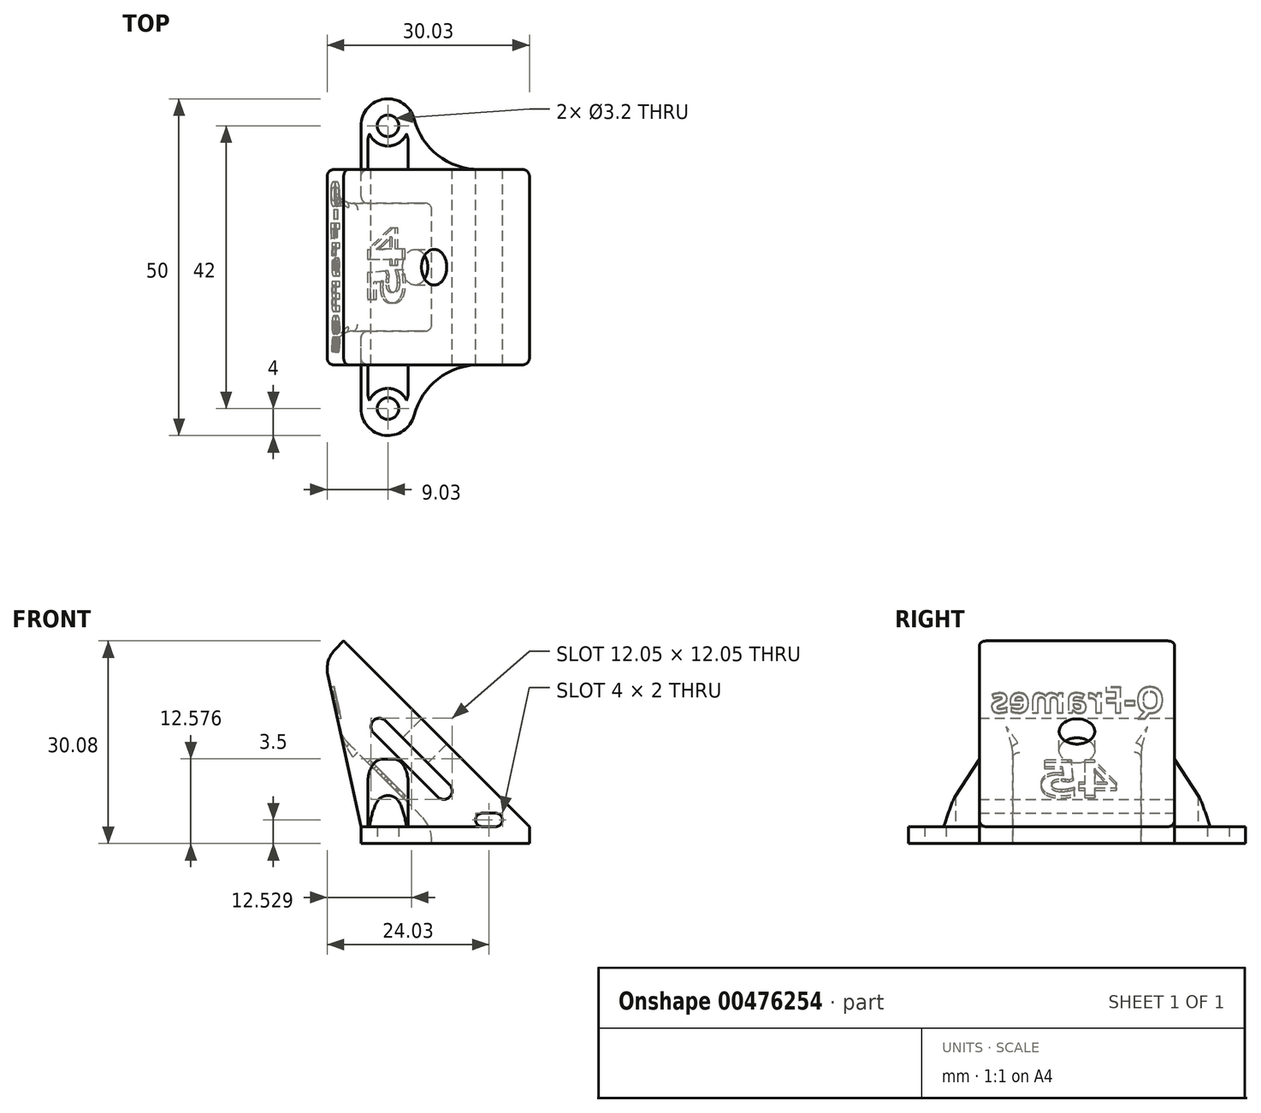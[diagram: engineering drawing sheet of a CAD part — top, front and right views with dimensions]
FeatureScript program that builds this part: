
annotation { "Feature Type Name" : "Feature", "Feature Type Description" : "" }
export const myFeature = defineFeature(function(context is Context, id is Id, definition is map)
    precondition{}
    {
        {
            var Q0;
            Q0=qCreatedBy(makeId("Front.planeOp"),FACE);
            var sketch = newSketch(context, id + "F0", { "sketchPlane" : qUnion([Q0])});
            skLineSegment(sketch, "E0", {"start": v(-27.58, 30.08) * mm, "end": v(0, 2.5) * mm});
            skLineSegment(sketch, "E1", {"start": v(-27.58, 30.08) * mm, "end": v(-28.86, 28.8) * mm});
            skLineSegment(sketch, "E2", {"start": v(-29.94, 25.11) * mm, "end": v(-25, 2.5) * mm});
            skLineSegment(sketch, "E3", {"start": v(0, 0) * mm, "end": v(0, 2.5) * mm});
            skLineSegment(sketch, "E4", {"start": v(-23.16, 18.23) * mm, "end": v(-23.16, 18.23) * mm});
            skLineSegment(sketch, "E5", {"start": v(-23.16, 16.47) * mm, "end": v(-13.61, 6.92) * mm});
            skLineSegment(sketch, "E6", {"start": v(-11.84, 6.92) * mm, "end": v(-11.84, 6.92) * mm});
            skLineSegment(sketch, "E7", {"start": v(-11.84, 8.69) * mm, "end": v(-21.39, 18.23) * mm});
            skLineSegment(sketch, "E8", {"start": v(-13.79, 16.29) * mm, "end": v(-16.62, 13.46) * mm, "construction": true});
            skPoint(sketch, "E9.visualSharp", {"position": v(-22.27, 19.12) * mm});
            skArc(sketch, "E9.filletArc", {"start": v(-21.39, 18.23) * mm, "mid": v(-22.27, 18.6) * mm, "end": v(-23.16, 18.23) * mm});
            skPoint(sketch, "E10.visualSharp", {"position": v(-10.96, 7.8) * mm});
            skArc(sketch, "E10.filletArc", {"start": v(-11.84, 6.92) * mm, "mid": v(-11.48, 7.8) * mm, "end": v(-11.84, 8.69) * mm});
            skPoint(sketch, "E11.visualSharp", {"position": v(-12.73, 6.04) * mm});
            skArc(sketch, "E11.filletArc", {"start": v(-13.61, 6.92) * mm, "mid": v(-12.73, 6.55) * mm, "end": v(-11.84, 6.92) * mm});
            skPoint(sketch, "E12.visualSharp", {"position": v(-24.04, 17.35) * mm});
            skArc(sketch, "E12.filletArc", {"start": v(-23.16, 18.23) * mm, "mid": v(-23.52, 17.35) * mm, "end": v(-23.16, 16.47) * mm});
            skLineSegment(sketch, "E13", {"start": v(-7, 3.5) * mm, "end": v(-5, 3.5) * mm, "construction": true});
            skArc(sketch, "E14.0.startCap", {"start": v(-7, 2.5) * mm, "mid": v(-8, 3.5) * mm, "end": v(-7, 4.5) * mm});
            skArc(sketch, "E14.0.endCap", {"start": v(-5, 4.5) * mm, "mid": v(-4, 3.5) * mm, "end": v(-5, 2.5) * mm});
            skLineSegment(sketch, "E14.0.left", {"start": v(-7, 4.5) * mm, "end": v(-5, 4.5) * mm});
            skLineSegment(sketch, "E14.0.right", {"start": v(-7, 2.5) * mm, "end": v(-5, 2.5) * mm});
            skPoint(sketch, "E15.visualSharp", {"position": v(-30.4, 27.25) * mm});
            skArc(sketch, "E15.filletArc", {"start": v(-28.86, 28.8) * mm, "mid": v(-29.87, 27.1) * mm, "end": v(-29.94, 25.11) * mm});
            skLineSegment(sketch, "E16", {"start": v(0, 0) * mm, "end": v(-25, 0) * mm});
            skLineSegment(sketch, "E17", {"start": v(-25, 2.5) * mm, "end": v(-25, 0) * mm});
            skSolve(sketch);
        }
        {
            var Q0;
            Q0=makeQuery(id+"F0.imprint","IMPRINT",FACE,{"disambiguationData":[TD([[makeQuery(id+"F0.imprint","IMPRINT",EDGE,{"derivedFrom":sQuery(id+"F0.wireOp",EDGE,"E0")}),-1.0]])]});
            extrude(context, id + "F1", {"entities" : qUnion([Q0]), "endBound" : BoundingType.SYMMETRIC, "depth" : 29 * mm, "offsetDistance" : 25 * mm});
        }
        {
            var Q0;
            Q0=makeQuery(id+"F1.opExtrude","SWEPT_FACE",FACE,{"disambiguationData":[OSD([sQuery(id+"F0.wireOp",EDGE,"E0")])]});
            var sketch = newSketch(context, id + "F2", { "sketchPlane" : qUnion([Q0])});
            skCircle(sketch, "E18", {"center": v(0, 21.77) * mm, "radius": 2.65 * mm});
            skSolve(sketch);
        }
        {
            var Q0;
            Q0=makeQuery(id+"F2.imprint","IMPRINT",FACE,{"disambiguationData":[TD([[makeQuery(id+"F2.imprint","IMPRINT",EDGE,{"derivedFrom":sQuery(id+"F2.wireOp",EDGE,"E18")}),1.0]])]});
            extrude(context, id + "F3", {"entities" : qUnion([Q0]), "operationType" : NewBodyOperationType.REMOVE, "oppositeDirection" : true, "depth" : 4.5 * mm, "offsetDistance" : 25 * mm});
        }
        {
            var Q0;
            Q0=makeQuery(id+"F1.opExtrude","SWEPT_FACE",FACE,{"disambiguationData":[OSD([sQuery(id+"F0.wireOp",EDGE,"E16")])]});
            var sketch = newSketch(context, id + "F4", { "sketchPlane" : qUnion([Q0])});
            skCircle(sketch, "E19", {"center": v(-21, 21) * mm, "radius": 1.6 * mm});
            skArc(sketch, "E20", {"start": v(-17.13, 22) * mm, "mid": v(-21.5, 24.97) * mm, "end": v(-25, 21) * mm});
            skCircle(sketch, "E21.MirrorC", {"center": v(-21, -21) * mm, "radius": 1.6 * mm});
            skLineSegment(sketch, "E22", {"start": v(-25, 21) * mm, "end": v(-25, -21) * mm});
            skArc(sketch, "E23", {"start": v(-17.13, 22) * mm, "mid": v(-13.57, 16.6) * mm, "end": v(-7.44, 14.5) * mm});
            skLineSegment(sketch, "E24", {"start": v(-7.44, 14.5) * mm, "end": v(-7.44, -14.5) * mm});
            skArc(sketch, "E25.MirrorCS", {"start": v(-17.13, -22) * mm, "mid": v(-21.5, -24.97) * mm, "end": v(-25, -21) * mm});
            skArc(sketch, "E26.MirrorCS", {"start": v(-17.13, -22) * mm, "mid": v(-13.57, -16.6) * mm, "end": v(-7.44, -14.5) * mm});
            skSolve(sketch);
        }
        {
            var Q0;
            Q0 = qSketchRegion(id + "F4", true);
            extrude(context, id + "F5", {"entities" : qUnion([Q0]), "operationType" : NewBodyOperationType.ADD, "oppositeDirection" : true, "depth" : 2.5 * mm, "offsetDistance" : 25 * mm});
        }
        {
            var Q0;
            Q0=makeQuery(id+"F1.opExtrude","CAP_EDGE",EDGE,{"disambiguationData":[OSD([sQuery(id+"F0.wireOp",EDGE,"E3")])],"isStart":false});
            var Q1;
            Q1=makeQuery(id+"F1.opExtrude","CAP_EDGE",EDGE,{"disambiguationData":[OSD([sQuery(id+"F0.wireOp",EDGE,"E3")])],"isStart":true});
            var Q2;
            Q2=makeQuery(id+"F1.opExtrude","CAP_EDGE",EDGE,{"disambiguationData":[OSD([sQuery(id+"F0.wireOp",EDGE,"E1")])],"isStart":false});
            var Q3;
            Q3=makeQuery(id+"F1.opExtrude","CAP_EDGE",EDGE,{"disambiguationData":[OSD([sQuery(id+"F0.wireOp",EDGE,"E1")])],"isStart":true});
            fillet(context, id + "F6", {"entities" : qUnion([Q0, Q1, Q2, Q3]), "radius" : 1 * mm, "tangentPropagation" : true, "allowEdgeOverflow" : false});
        }
        {
            var Q0;
            Q0=qCreatedBy(makeId("Front.planeOp"),FACE);
            var sketch = newSketch(context, id + "F7", { "sketchPlane" : qUnion([Q0])});
            skLineSegment(sketch, "E27", {"start": v(-14.5, 0) * mm, "end": v(-14.5, 2.5) * mm});
            skLineSegment(sketch, "E28", {"start": v(-14.5, 2.5) * mm, "end": v(-34.5, 22.5) * mm});
            skLineSegment(sketch, "E29", {"start": v(-34.5, 22.5) * mm, "end": v(-34.5, 0) * mm});
            skLineSegment(sketch, "E30", {"start": v(-34.5, 0) * mm, "end": v(-14.5, 0) * mm});
            skSolve(sketch);
        }
        {
            var Q0;
            Q0=makeQuery(id+"F7.imprint","IMPRINT",FACE,{"disambiguationData":[TD([[makeQuery(id+"F7.imprint","IMPRINT",EDGE,{"derivedFrom":sQuery(id+"F7.wireOp",EDGE,"E27")}),1.0]])]});
            extrude(context, id + "F8", {"entities" : qUnion([Q0]), "operationType" : NewBodyOperationType.REMOVE, "endBound" : BoundingType.SYMMETRIC, "depth" : 19 * mm, "offsetDistance" : 25 * mm});
        }
        {
            var Q0;
            Q0=makeQuery(id+"F8.boolean.opBoolean","INTERSECT",EDGE,{"derivedFrom":[makeQuery(id+"F1.opExtrude","SWEPT_FACE",FACE,{"disambiguationData":[OSD([sQuery(id+"F0.wireOp",EDGE,"E2")])]}),makeQuery(id+"F8.opExtrude","SWEPT_FACE",FACE,{"disambiguationData":[OSD([sQuery(id+"F7.wireOp",EDGE,"E28")])]})]});
            var Q1;
            Q1=makeQuery(id+"F8.boolean.opBoolean","COPY",EDGE,{"derivedFrom":makeQuery(id+"F8.opExtrude","SWEPT_EDGE",EDGE,{"disambiguationData":[OSD([sQuery(id+"F7.wireOp",EDGE,"E27"),sQuery(id+"F7.wireOp",EDGE,"E28")])]})});
            fillet(context, id + "F9", {"entities" : qUnion([Q0, Q1]), "radius" : 5 * mm, "tangentPropagation" : true, "allowEdgeOverflow" : false});
        }
        {
            var Q0;
            Q0=makeQuery(id+"F8.boolean.opBoolean","INTERSECT",EDGE,{"derivedFrom":[makeQuery(id+"F1.opExtrude","SWEPT_FACE",FACE,{"disambiguationData":[OSD([sQuery(id+"F0.wireOp",EDGE,"E2")])]}),makeQuery(id+"F8.opExtrude","CAP_FACE",FACE,{"disambiguationData":[OSD([sQuery(id+"F7.wireOp",EDGE,"E27"),sQuery(id+"F7.wireOp",EDGE,"E28"),sQuery(id+"F7.wireOp",EDGE,"E29"),sQuery(id+"F7.wireOp",EDGE,"E30")])],"isStart":true})]});
            var Q1;
            Q1=makeQuery(id+"F8.boolean.opBoolean","INTERSECT",EDGE,{"derivedFrom":[makeQuery(id+"F1.opExtrude","SWEPT_FACE",FACE,{"disambiguationData":[OSD([sQuery(id+"F0.wireOp",EDGE,"E2")])]}),makeQuery(id+"F8.opExtrude","CAP_FACE",FACE,{"disambiguationData":[OSD([sQuery(id+"F7.wireOp",EDGE,"E27"),sQuery(id+"F7.wireOp",EDGE,"E28"),sQuery(id+"F7.wireOp",EDGE,"E29"),sQuery(id+"F7.wireOp",EDGE,"E30")])],"isStart":false})]});
            var Q2;
            Q2=makeQuery(id+"F8.boolean.opBoolean","INTERSECT",EDGE,{"derivedFrom":[makeQuery(id+"F5.boolean.opBoolean","MERGE",FACE,{"derivedFrom":[makeQuery(id+"F1.opExtrude","SWEPT_FACE",FACE,{"disambiguationData":[OSD([sQuery(id+"F0.wireOp",EDGE,"E17")])]}),makeQuery(id+"F5.opExtrude","SWEPT_FACE",FACE,{"disambiguationData":[OSD([sQuery(id+"F4.wireOp",EDGE,"E22")])]})]}),makeQuery(id+"F8.opExtrude","CAP_FACE",FACE,{"disambiguationData":[OSD([sQuery(id+"F7.wireOp",EDGE,"E27"),sQuery(id+"F7.wireOp",EDGE,"E28"),sQuery(id+"F7.wireOp",EDGE,"E29"),sQuery(id+"F7.wireOp",EDGE,"E30")])],"isStart":true})]});
            var Q3;
            Q3=makeQuery(id+"F8.boolean.opBoolean","INTERSECT",EDGE,{"derivedFrom":[makeQuery(id+"F5.boolean.opBoolean","MERGE",FACE,{"derivedFrom":[makeQuery(id+"F1.opExtrude","SWEPT_FACE",FACE,{"disambiguationData":[OSD([sQuery(id+"F0.wireOp",EDGE,"E17")])]}),makeQuery(id+"F5.opExtrude","SWEPT_FACE",FACE,{"disambiguationData":[OSD([sQuery(id+"F4.wireOp",EDGE,"E22")])]})]}),makeQuery(id+"F8.opExtrude","CAP_FACE",FACE,{"disambiguationData":[OSD([sQuery(id+"F7.wireOp",EDGE,"E27"),sQuery(id+"F7.wireOp",EDGE,"E28"),sQuery(id+"F7.wireOp",EDGE,"E29"),sQuery(id+"F7.wireOp",EDGE,"E30")])],"isStart":false})]});
            fillet(context, id + "F10", {"entities" : qUnion([Q0, Q1, Q2, Q3]), "radius" : 1 * mm, "tangentPropagation" : true, "allowEdgeOverflow" : false});
        }
        {
            var Q0;
            Q0=makeQuery(id+"F8.boolean.opBoolean","COPY",FACE,{"derivedFrom":makeQuery(id+"F8.opExtrude","SWEPT_FACE",FACE,{"disambiguationData":[OSD([sQuery(id+"F7.wireOp",EDGE,"E28")])]})});
            fillet(context, id + "F11", {"entities" : qUnion([Q0]), "radius" : 1 * mm, "tangentPropagation" : true, "allowEdgeOverflow" : false});
        }
        {
            var Q0;
            Q0=makeQuery(id+"F1.opExtrude","SWEPT_FACE",FACE,{"disambiguationData":[OSD([sQuery(id+"F0.wireOp",EDGE,"E2")])]});
            var sketch = newSketch(context, id + "F12", { "sketchPlane" : qUnion([Q0])});
            skText(sketch, "E31", { "text": "Q-Frames", "fontName": "OpenSans-Bold.ttf"});
            const initialGuessF12  = {"E31": [-0.013, 0.02504, 1, 0, 0.00388]};
            skSetInitialGuess(sketch, initialGuessF12);
            skSolve(sketch);
        }
        {
            var Q0;
            Q0 = qSketchRegion(id + "F12", true);
            extrude(context, id + "F13", {"entities" : qUnion([Q0]), "operationType" : NewBodyOperationType.REMOVE, "oppositeDirection" : true, "depth" : 0.5 * mm, "offsetDistance" : 25 * mm});
        }
        {
            var Q0;
            Q0=makeQuery(id+"F8.boolean.opBoolean","COPY",FACE,{"derivedFrom":makeQuery(id+"F8.opExtrude","SWEPT_FACE",FACE,{"disambiguationData":[OSD([sQuery(id+"F7.wireOp",EDGE,"E28")])]})});
            var sketch = newSketch(context, id + "F14", { "sketchPlane" : qUnion([Q0])});
            skText(sketch, "E32", { "text": "45", "fontName": "OpenSans-Bold.ttf"});
            const initialGuessF14  = {"E32": [-0.006, 0.01812, 1, 0, 0.00744]};
            skSetInitialGuess(sketch, initialGuessF14);
            skSolve(sketch);
        }
        {
            var Q0;
            Q0 = qSketchRegion(id + "F14", true);
            extrude(context, id + "F15", {"entities" : qUnion([Q0]), "operationType" : NewBodyOperationType.REMOVE, "oppositeDirection" : true, "depth" : 0.5 * mm, "offsetDistance" : 25 * mm});
        }
        {
            var Q0;
            {var subQ4=sQuery(id+"F4.wireOp",EDGE,"E22");var subQ6=sQuery(id+"F4.wireOp",EDGE,"E20");Q0=makeQuery(id+"F8.boolean.opBoolean","SPLIT",FACE,{"disambiguationData":[TD([makeQuery(id+"F5.opExtrude","SWEPT_FACE",FACE,{"disambiguationData":[OSD([subQ6])]})])],"derivedFrom":makeQuery(id+"F5.boolean.opBoolean","MERGE",FACE,{"derivedFrom":[makeQuery(id+"F1.opExtrude","SWEPT_FACE",FACE,{"disambiguationData":[OSD([sQuery(id+"F0.wireOp",EDGE,"E17")])]}),makeQuery(id+"F5.opExtrude","SWEPT_FACE",FACE,{"disambiguationData":[OSD([subQ4])]})]})});}
            var sketch = newSketch(context, id + "F16", { "sketchPlane" : qUnion([Q0])});
            skLineSegment(sketch, "E33", {"start": v(-21, 2.5) * mm, "end": v(-14.5, 12.5) * mm});
            skLineSegment(sketch, "E34", {"start": v(-14.5, 12.5) * mm, "end": v(-14.5, 2.5) * mm});
            skLineSegment(sketch, "E35", {"start": v(-14.5, 2.5) * mm, "end": v(-21, 2.5) * mm});
            skSolve(sketch);
        }
        {
            var Q0;
            Q0=makeQuery(id+"F16.imprint","IMPRINT",FACE,{"disambiguationData":[TD([[makeQuery(id+"F16.imprint","IMPRINT",EDGE,{"derivedFrom":sQuery(id+"F16.wireOp",EDGE,"E33")}),-1.0]])]});
            extrude(context, id + "F17", {"entities" : qUnion([Q0]), "oppositeDirection" : true, "depth" : 7 * mm, "offsetDistance" : 25 * mm, "hasSecondDirection" : true, "secondDirectionOppositeDirection" : true, "secondDirectionDepth" : 1 * mm});
        }
        {
            var Q0;
            Q0=makeQuery(id+"F17.opExtrude","SWEPT_BODY",BODY,{"disambiguationData":[OSD([sQuery(id+"F16.wireOp",EDGE,"E33"),sQuery(id+"F16.wireOp",EDGE,"E34"),sQuery(id+"F16.wireOp",EDGE,"E35")])]});
            var Q1;
            Q1=qCreatedBy(makeId("Front.planeOp"),FACE);
            mirror(context, id + "F18", {"operationType" : NewBodyOperationType.ADD, "entities" : qUnion([Q0]), "mirrorPlane" : qUnion([Q1])});
        }
        {
            var Q0;
            {var subQ0=sQuery(id+"F4.wireOp",EDGE,"E21.MirrorC");var subQ2=sQuery(id+"F4.wireOp",EDGE,"E22");var subQ4=sQuery(id+"F4.wireOp",EDGE,"E25.MirrorCS");var subQ5=sQuery(id+"F4.wireOp",EDGE,"E26.MirrorCS");Q0=makeQuery(id+"F5.boolean.opBoolean","SPLIT",FACE,{"disambiguationData":[TD([makeQuery(id+"F5.opExtrude","SWEPT_FACE",FACE,{"disambiguationData":[OSD([subQ0])]})])],"derivedFrom":makeQuery(id+"F5.opExtrude","CAP_FACE",FACE,{"disambiguationData":[OSD([sQuery(id+"F4.wireOp",EDGE,"E19"),sQuery(id+"F4.wireOp",EDGE,"E20"),subQ0,subQ2,sQuery(id+"F4.wireOp",EDGE,"E23"),sQuery(id+"F4.wireOp",EDGE,"E24"),subQ4,subQ5])],"isStart":false})});}
            var sketch = newSketch(context, id + "F19", { "sketchPlane" : qUnion([Q0])});
            skCircle(sketch, "E36", {"center": v(-21, 21) * mm, "radius": 3 * mm});
            skCircle(sketch, "E37", {"center": v(-21, -21) * mm, "radius": 3 * mm});
            skSolve(sketch);
        }
        {
            var Q0;
            Q0=makeQuery(id+"F17.opExtrude","CAP_EDGE",EDGE,{"disambiguationData":[OSD([sQuery(id+"F16.wireOp",EDGE,"E33")])],"isStart":true});
            var Q1;
            Q1=makeQuery(id+"F17.opExtrude","CAP_EDGE",EDGE,{"disambiguationData":[OSD([sQuery(id+"F16.wireOp",EDGE,"E33")])],"isStart":false});
            var Q2;
            Q2=makeQuery(id+"F18.opPattern","COPY",EDGE,{"derivedFrom":makeQuery(id+"F17.opExtrude","CAP_EDGE",EDGE,{"disambiguationData":[OSD([sQuery(id+"F16.wireOp",EDGE,"E33")])],"isStart":true}),"instanceName":"1"});
            var Q3;
            Q3=makeQuery(id+"F18.opPattern","COPY",EDGE,{"derivedFrom":makeQuery(id+"F17.opExtrude","CAP_EDGE",EDGE,{"disambiguationData":[OSD([sQuery(id+"F16.wireOp",EDGE,"E33")])],"isStart":false}),"instanceName":"1"});
            fillet(context, id + "F20", {"entities" : qUnion([Q0, Q1, Q2, Q3]), "radius" : 2 * mm, "tangentPropagation" : true, "allowEdgeOverflow" : false});
        }
        {
            var Q0;
            Q0 = qSketchRegion(id + "F19", true);
            extrude(context, id + "F21", {"entities" : qUnion([Q0]), "operationType" : NewBodyOperationType.REMOVE, "depth" : 25 * mm, "offsetDistance" : 25 * mm});
        }
    });
